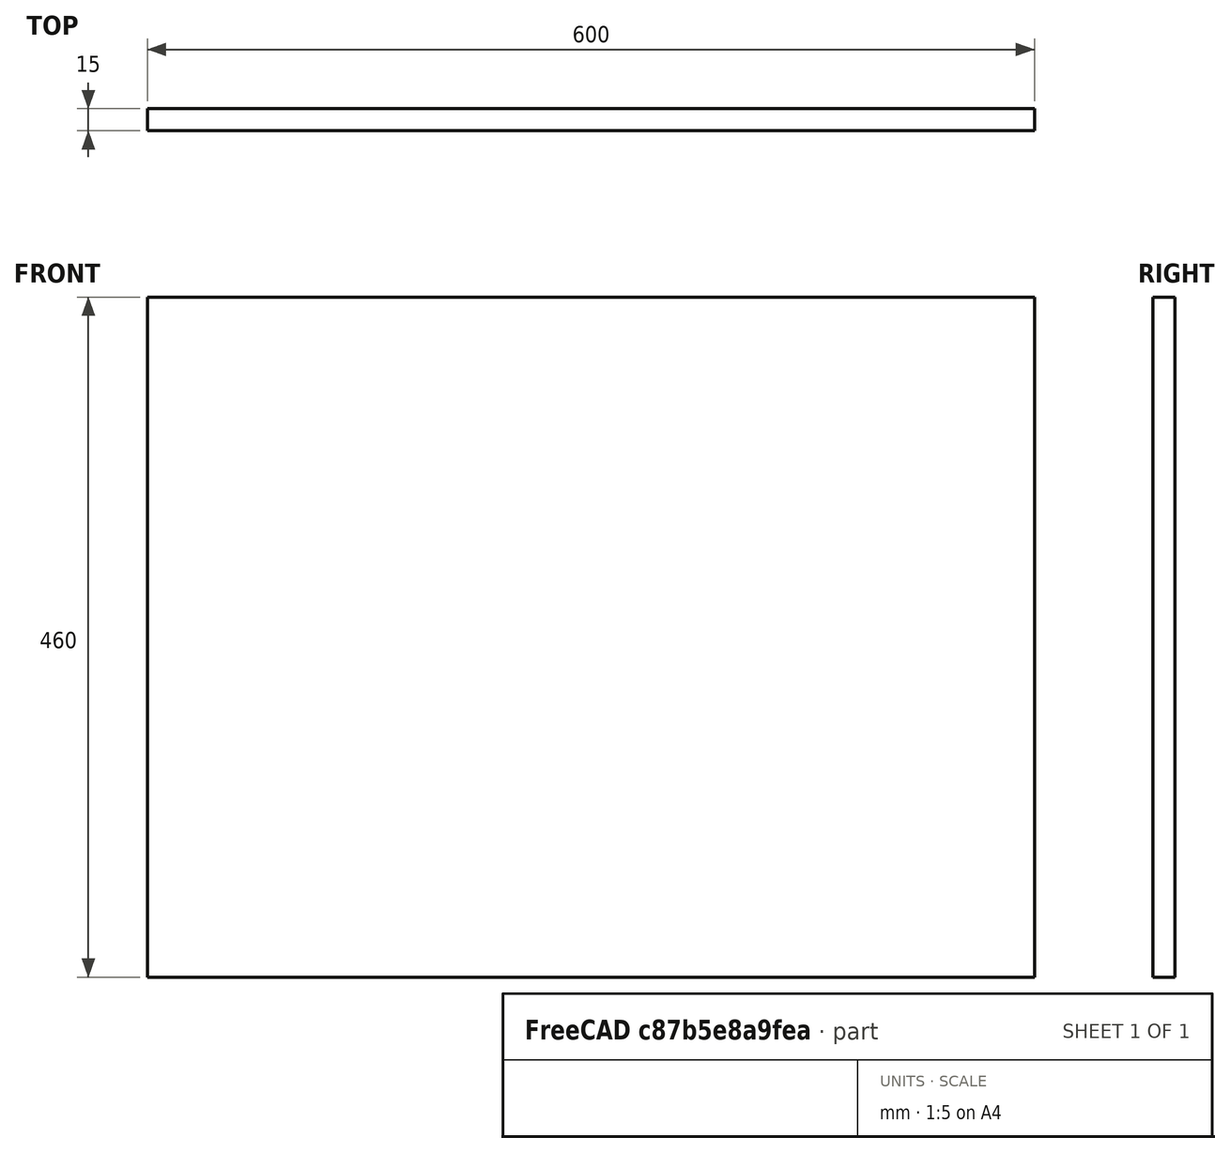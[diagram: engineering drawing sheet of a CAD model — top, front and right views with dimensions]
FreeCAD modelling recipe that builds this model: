
FCSTD DOCUMENT  (FreeCAD 1.0R39319 (Git))
Label: back_top_door
License: All rights reserved
LicenseURL: https://en.wikipedia.org/wiki/All_rights_reserved
objects: Sketcher::SketchObject×1, PartDesign::Pad×1, PartDesign::Body×1
note: 6 computed .brp shape members not serialized (recipe doc carries the construction recipe); baked Part::Feature solids carry a one-line shape summary decoded from their .brp

FEATURE [Sketcher::SketchObject] Sketch  label="back_top_door_s"
  ArcFitTolerance = 1e-06
  AttachmentSupport = -> [XZ_Plane]
  FullyConstrained = true
  MakeInternals = false
  MapMode = 5
  Placement = pos=(0,0,0) rot=(1,0,0;1.5708rad)
  sketch-geometry (4):
    g0: LineSegment StartX=0 StartY=0 StartZ=0 EndX=600 EndY=0 EndZ=0
    g1: LineSegment StartX=600 StartY=0 StartZ=0 EndX=600 EndY=460 EndZ=0
    g2: LineSegment StartX=600 StartY=460 StartZ=0 EndX=0 EndY=460 EndZ=0
    g3: LineSegment StartX=0 StartY=460 StartZ=0 EndX=0 EndY=0 EndZ=0
  constraints (11):
    c: Coincident(g0,g1)
    c: Coincident(g1,g2)
    c: Coincident(g2,g3)
    c: Coincident(g3,g0)
    c: Horizontal(g0)
    c: Horizontal(g2)
    c: Vertical(g1)
    c: Vertical(g3)
    c: Coincident(g0,g-1)
    c: DistanceX(g2,g2) = 600
    c: DistanceY(g3,g3) = 460
FEATURE [PartDesign::Pad] Pad  label="back_top_door"
  Direction = (0,-1,2e-16)
  Length = 15
  Length2 = 10
  Placement = pos=(0,0,0) rot=(1,0,0;1.5708rad)
  Profile = -> Sketch
  ReferenceAxis = -> Sketch [N_Axis]
  Refine = true
  Suppressed = false
  Type = 0
FEATURE [PartDesign::Body] Body  label="back_top_door_body"
  AllowCompound = false
  Group = -> [Sketch,Pad]
  Origin = -> Origin
  Tip = -> Pad
